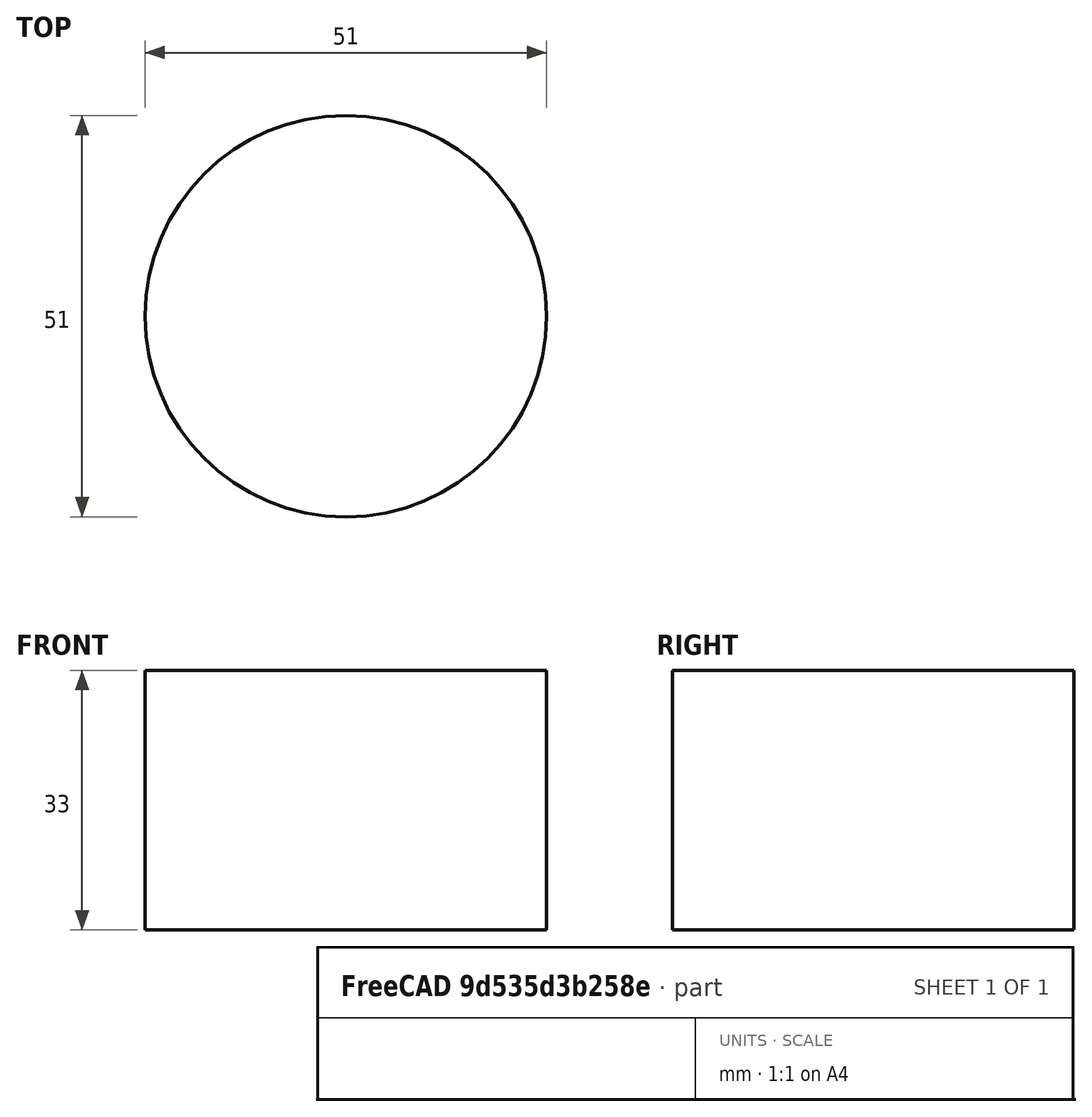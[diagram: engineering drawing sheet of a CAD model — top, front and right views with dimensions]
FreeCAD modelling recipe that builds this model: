
FCSTD DOCUMENT  (FreeCAD 0.17R13509 (Git))
Label: rf_ftinsulator
License: All rights reserved
LicenseURL: http://en.wikipedia.org/wiki/All_rights_reserved
objects: Part::Cylinder×10, Part::MultiFuse×5, Path::FeaturePython×5, Part::Box×2, Part::Cut×2, Part::FeaturePython×2, App::FeaturePython×1, Path::FeatureCompoundPython×1
note: 24 computed .brp shape members not serialized (recipe doc carries the construction recipe); baked Part::Feature solids carry a one-line shape summary decoded from their .brp

FEATURE [Part::Cylinder] Cylinder111  label="RFFeeds007"
  Angle = 360
  AttacherType = Attacher::AttachEngine3D
  Height = 5
  Placement = pos=(86.69,175.69,-5) rot=(0,0,1;0rad)
  Radius = 10
  expr: Placement.Base.x = 105 - 18.309999999999999
  expr: Placement.Base.y = 194 - 18.309999999999999
FEATURE [Part::Cylinder] Cylinder112  label="RFFeeds008"
  Angle = 360
  AttacherType = Attacher::AttachEngine3D
  Height = 46
  Placement = pos=(86.69,175.69,-14) rot=(0,0,1;0rad)
  Radius = 5.3
  expr: Placement.Base.x = 105 - 18.309999999999999
  expr: Placement.Base.y = 194 - 18.309999999999999
FEATURE [Part::Box] Box019  label="RFFeedLug001"
  AttacherType = Attacher::AttachEngine3D
  Height = 1
  Length = 1
  Placement = pos=(77.69,174.69,-5) rot=(0,0,1;0rad)
  Width = 1
FEATURE [Part::Cylinder] Cylinder113  label="FTThreaded007"
  Angle = 360
  AttacherType = Attacher::AttachEngine3D
  Height = 11
  Placement = pos=(73.69,175.69,-10) rot=(0,0,1;0rad)
  Radius = 1.5
FEATURE [Part::Cylinder] Cylinder114  label="FTThreaded008"
  Angle = 360
  AttacherType = Attacher::AttachEngine3D
  Height = 11
  Placement = pos=(99.69,175.69,-10) rot=(0,0,1;0rad)
  Radius = 1.5
FEATURE [Part::MultiFuse] Fusion048
  Shapes = -> [Cylinder113,Cylinder114,Cylinder112]
FEATURE [Part::Cylinder] Cylinder115  label="RFFeeds009"
  Angle = 360
  AttacherType = Attacher::AttachEngine3D
  Height = 33
  Placement = pos=(86.69,175.69,-5) rot=(0,0,1;0rad)
  Radius = 7
  expr: Placement.Base.x = 105 - 18.309999999999999
  expr: Placement.Base.y = 194 - 18.309999999999999
FEATURE [Part::MultiFuse] Fusion047
  Shapes = -> [Cylinder115,Box019,Cylinder111]
FEATURE [Part::Cut] Cut014  label="RFFTInsulator002"
  Base = -> Fusion047
  Placement = pos=(-86.69,-189.69,-28) rot=(0,0,1;0rad)
  Tool = -> Fusion048
FEATURE [Part::Cylinder] Cylinder116  label="FTThreaded009"
  Angle = 360
  AttacherType = Attacher::AttachEngine3D
  Height = 11
  Placement = pos=(73.69,175.69,-10) rot=(0,0,1;0rad)
  Radius = 1.5
FEATURE [Part::Box] Box020  label="RFFeedLug002"
  AttacherType = Attacher::AttachEngine3D
  Height = 1
  Length = 1
  Placement = pos=(77.69,174.69,-5) rot=(0,0,1;0rad)
  Width = 1
FEATURE [Part::Cylinder] Cylinder117  label="RFFeeds010"
  Angle = 360
  AttacherType = Attacher::AttachEngine3D
  Height = 5
  Placement = pos=(86.69,175.69,-5) rot=(0,0,1;0rad)
  Radius = 10
  expr: Placement.Base.x = 105 - 18.309999999999999
  expr: Placement.Base.y = 194 - 18.309999999999999
FEATURE [Part::Cylinder] Cylinder118  label="FTThreaded010"
  Angle = 360
  AttacherType = Attacher::AttachEngine3D
  Height = 11
  Placement = pos=(99.69,175.69,-10) rot=(0,0,1;0rad)
  Radius = 1.5
FEATURE [Part::Cylinder] Cylinder119  label="RFFeeds011"
  Angle = 360
  AttacherType = Attacher::AttachEngine3D
  Height = 46
  Placement = pos=(86.69,175.69,-14) rot=(0,0,1;0rad)
  Radius = 5.2
  expr: Placement.Base.x = 105 - 18.309999999999999
  expr: Placement.Base.y = 194 - 18.309999999999999
FEATURE [Part::MultiFuse] Fusion050
  Shapes = -> [Cylinder116,Cylinder118,Cylinder119]
FEATURE [Part::Cylinder] Cylinder120  label="RFFeeds012"
  Angle = 360
  AttacherType = Attacher::AttachEngine3D
  Height = 33
  Placement = pos=(86.69,175.69,-5) rot=(0,0,1;0rad)
  Radius = 7
  expr: Placement.Base.x = 105 - 18.309999999999999
  expr: Placement.Base.y = 194 - 18.309999999999999
FEATURE [Part::MultiFuse] Fusion049
  Shapes = -> [Cylinder120,Box020,Cylinder117]
FEATURE [Part::Cut] Cut015  label="RFFTInsulator003"
  Base = -> Fusion049
  Placement = pos=(-86.69,-161.69,-28) rot=(0,0,1;0rad)
  Tool = -> Fusion050
FEATURE [Part::MultiFuse] Fusion
  Shapes = -> [Cut014,Cut015]
FEATURE [App::FeaturePython] SetupSheet  # Path/CAM operation (typed FeaturePython)
  ClearanceHeightExpression = StartDepth+SetupSheet.ClearanceHeightOffset
  ClearanceHeightOffset = 5
  FinalDepthExpression = OpFinalDepth
  HorizRapid = 0
  SafeHeightExpression = StartDepth+SetupSheet.SafeHeightOffset
  SafeHeightOffset = 3
  StartDepthExpression = OpStartDepth
  StepDownExpression = OpToolDiameter
  VertRapid = 0
FEATURE [Part::FeaturePython] Clone  label="Base-Fusion"  # Draft clone (typed FeaturePython)
  AttacherType = Attacher::AttachEngine3D
  Fuse = false
  Objects = -> [Fusion]
  PathResource = Base
  Scale = (1,1,1)
FEATURE [Path::FeaturePython] T2__250_End_Mill  label="T2: 250 End Mill"  # Path/CAM operation (typed FeaturePython)
  HorizFeed = 1500
  HorizRapid = 0
  SpindleDir = 0
  SpindleSpeed = 24000
  ToolNumber = 2
  VertFeed = 40
  VertRapid = 0
  expr: HorizRapid = SetupSheet.HorizRapid
  expr: VertRapid = SetupSheet.VertRapid
FEATURE [Part::FeaturePython] Stock001  # WARN: FeaturePython — macro-defined, semantics opaque (R4)
  Height = 33
  Placement = pos=(0.0162135,0,-33) rot=(0,0,1;0rad)
  Radius = 25.5
  StockType = CreateCylinder
FEATURE [Path::FeaturePython] Contour  # Path/CAM operation (typed FeaturePython)
  Active = true
  AreaParams:
    OpenMode = 0
    Angle = 45.0
    MinArcPoints = 4
    Coplanar = 2
    Tolerance = 1e-07
    CleanDistance = 0.0
    PocketExtraOffset = 0.0
    RoundPrecision = 0.0
    AngleShift = 0.0
    SubjectFill = 0
    PocketMode = 0
    Simplify = False
    SectionTolerance = 1e-06
    MaxArcPoints = 100
    Offset = 3.175
    Accuracy = 0.01
    PocketStepover = 0.0
    ClipFill = 0
    ToolRadius = 1.0
    Outline = False
    ClipperScale = 10000000.0
    FromCenter = False
    Explode = False
    EndType = 0
    Shift = 0.0
    ExtraPass = 0
    Project = False
    JoinType = 0
    Thicken = False
    Stepdown = 1.0
    SectionMode = 2
    MiterLimit = 2.0
    Deflection = 0.01
    Reorient = True
    FitArcs = True
    SectionCount = -1
    SectionOffset = 0.0
    Stepover = 0.0
    Unit = 1.0
    Fill = 0
  ClearanceHeight = 5
  Direction = 0
  FinalDepth = -34
  JoinType = 0
  MiterLimit = 0.1
  OffsetExtra = 0
  OpFinalDepth = -33
  OpStartDepth = 0
  OpToolDiameter = 6.35
  PathParams = {'resume_height': 3.0, 'feedrate': 1500.0, 'verbose': True, 'orientation': 1, 'return_end': True, 'preamble': False, 'retraction': 5.0, 'feedrate_v': 40.0}
  SafeHeight = 3
  Side = 0
  StartDepth = 0
  StartPoint = (0,0,0)
  StepDown = 2
  ToolController = -> T2__250_End_Mill
  UseComp = true
  UseStartPoint = false
  expr: ClearanceHeight = StartDepth + SetupSheet.ClearanceHeightOffset
  expr: SafeHeight = StartDepth + SetupSheet.SafeHeightOffset
  expr: StepDown = 2
  expr: StartDepth = OpStartDepth
FEATURE [Path::FeaturePython] Pocket_Shape  # Path/CAM operation (typed FeaturePython)
  Active = true
  AreaParams:
    OpenMode = 0
    Angle = 45.0
    MinArcPoints = 4
    Coplanar = 0
    Tolerance = 1e-07
    CleanDistance = 0.0
    PocketExtraOffset = 0.0
    RoundPrecision = 0.0
    AngleShift = 0.0
    SubjectFill = 0
    PocketMode = 3
    Simplify = False
    SectionTolerance = 1e-06
    MaxArcPoints = 100
    Offset = 0.0
    Accuracy = 0.01
    PocketStepover = 3.175
    ClipFill = 0
    ToolRadius = 3.175
    Outline = False
    ClipperScale = 10000000.0
    FromCenter = True
    Explode = False
    EndType = 0
    Shift = 0.0
    ExtraPass = 0
    Project = False
    JoinType = 0
    Thicken = False
    Stepdown = 1.0
    SectionMode = 2
    MiterLimit = 2.0
    Deflection = 0.01
    Reorient = True
    FitArcs = True
    SectionCount = -1
    SectionOffset = 0.0
    Stepover = 0.0
    Unit = 1.0
    Fill = 0
  Base = -> [Clone]
  ClearanceHeight = 5
  CutMode = 1
  ExtraOffset = 0
  FinalDepth = -34
  FinishDepth = -1
  KeepToolDown = false
  MinTravel = false
  OffsetPattern = 2
  OpFinalDepth = -33
  OpStartDepth = 0
  OpToolDiameter = 6.35
  PathParams = {'resume_height': 3.0, 'feedrate': 1500.0, 'verbose': True, 'orientation': 0, 'return_end': True, 'preamble': False, 'retraction': 5.0, 'feedrate_v': 40.0}
  SafeHeight = 3
  StartAt = 0
  StartDepth = 0
  StartPoint = (0,0,0)
  StepDown = 2
  StepOver = 50
  ToolController = -> T2__250_End_Mill
  UseStartPoint = false
  ZigZagAngle = 45
  expr: ClearanceHeight = StartDepth + SetupSheet.ClearanceHeightOffset
  expr: SafeHeight = StartDepth + SetupSheet.SafeHeightOffset
  expr: StepDown = 2
  expr: FinalDepth = -34
  expr: StartDepth = OpStartDepth
FEATURE [Path::FeaturePython] MillFace  # Path/CAM operation (typed FeaturePython)
  Active = true
  AreaParams:
    OpenMode = 0
    Angle = 45.0
    MinArcPoints = 4
    Coplanar = 0
    Tolerance = 1e-07
    CleanDistance = 0.0
    PocketExtraOffset = 0.0
    RoundPrecision = 0.0
    AngleShift = 0.0
    SubjectFill = 0
    PocketMode = 3
    Simplify = False
    SectionTolerance = 1e-06
    MaxArcPoints = 100
    Offset = 0.0
    Accuracy = 0.01
    PocketStepover = 3.175
    ClipFill = 0
    ToolRadius = 3.175
    Outline = False
    ClipperScale = 10000000.0
    FromCenter = True
    Explode = False
    EndType = 0
    Shift = 0.0
    ExtraPass = 0
    Project = False
    JoinType = 0
    Thicken = False
    Stepdown = 1.0
    SectionMode = 2
    MiterLimit = 2.0
    Deflection = 0.01
    Reorient = True
    FitArcs = True
    SectionCount = -1
    SectionOffset = 0.0
    Stepover = 0.0
    Unit = 1.0
    Fill = 0
  Base = -> [Clone]
  BoundaryShape = 0
  ClearanceHeight = 9
  CutMode = 0
  ExtraOffset = 0
  FinalDepth = 0
  FinishDepth = 0
  KeepToolDown = false
  MinTravel = false
  OffsetPattern = 2
  OpFinalDepth = 0
  OpStartDepth = 2
  OpToolDiameter = 6.35
  PathParams = {'resume_height': 7.0, 'feedrate': 1500.0, 'verbose': True, 'orientation': 1, 'return_end': True, 'preamble': False, 'retraction': 9.0, 'feedrate_v': 40.0}
  SafeHeight = 7
  StartAt = 0
  StartDepth = 4
  StartPoint = (0,0,0)
  StepDown = 2
  StepOver = 50
  ToolController = -> T2__250_End_Mill
  UseStartPoint = false
  ZigZagAngle = 45
  expr: ClearanceHeight = StartDepth + SetupSheet.ClearanceHeightOffset
  expr: SafeHeight = StartDepth + SetupSheet.SafeHeightOffset
  expr: StepDown = 2
  expr: FinalDepth = OpFinalDepth
FEATURE [Path::FeatureCompoundPython] Operations  # Path/CAM operation (typed FeaturePython)
  Group = -> [Contour,Pocket_Shape,MillFace]
  UsePlacements = false
FEATURE [Path::FeaturePython] Job  # Path/CAM operation (typed FeaturePython)
  Base = -> Clone
  GeometryTolerance = 0.01
  Operations = -> Operations
  PostProcessor = 5
  PostProcessorOutputFile = <userpath>/Documents/CNC/chamber_plate/fts/RFInsulator1_250_roughing_NEW.ngc
  SetupSheet = -> SetupSheet
  Stock = -> Stock001
  ToolController = -> [T2__250_End_Mill]
